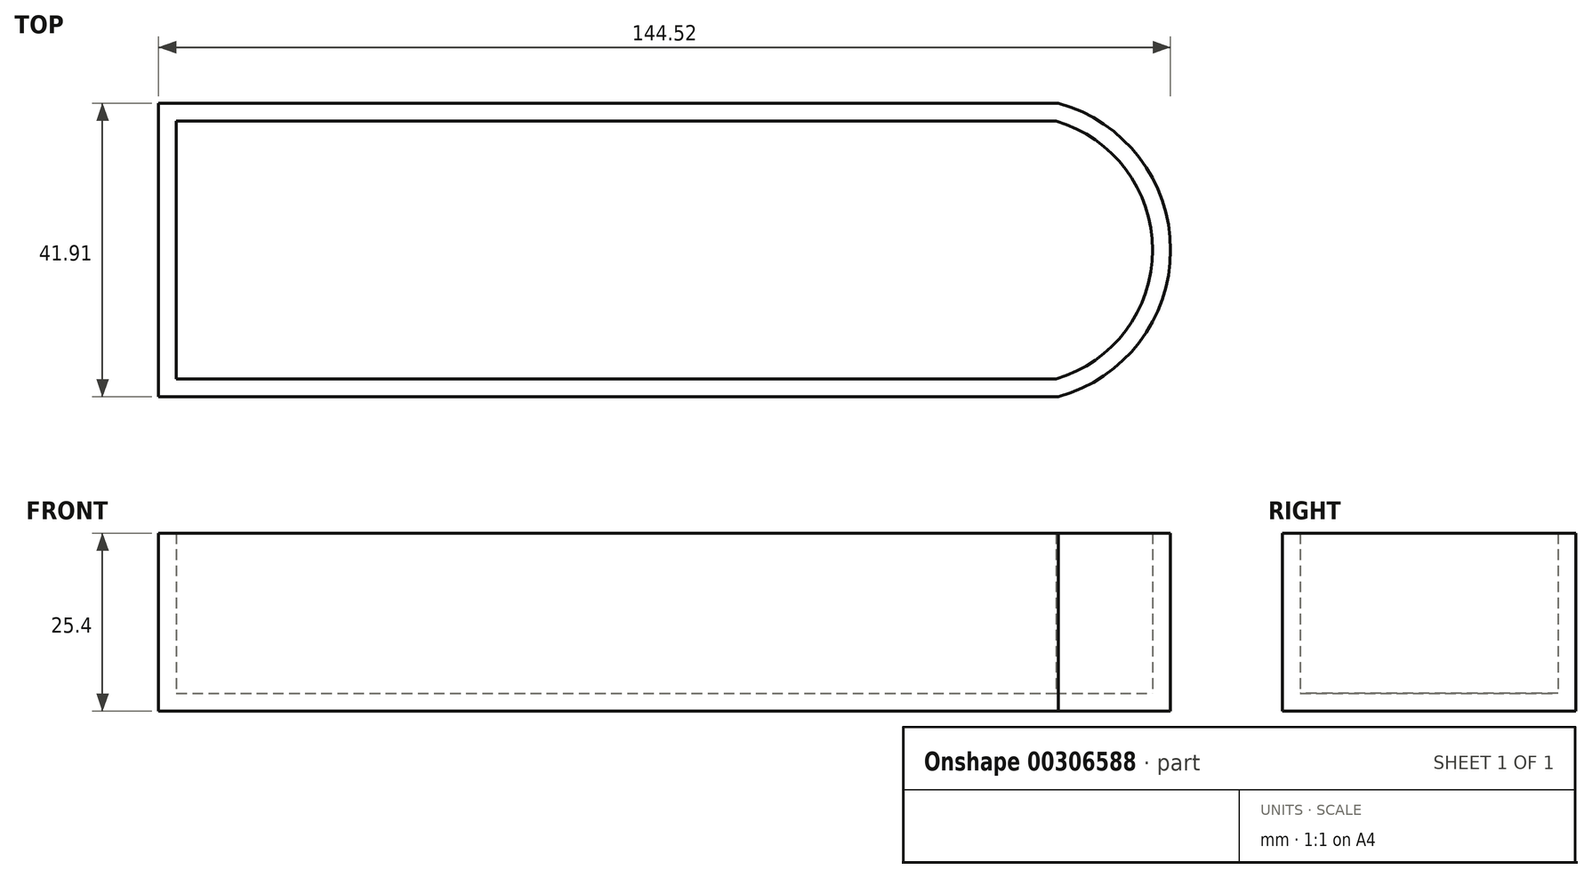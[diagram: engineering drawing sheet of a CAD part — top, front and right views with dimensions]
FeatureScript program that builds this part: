
annotation { "Feature Type Name" : "Feature", "Feature Type Description" : "" }
export const myFeature = defineFeature(function(context is Context, id is Id, definition is map)
    precondition{}
    {
        {
            var Q0;
            Q0=qCreatedBy(makeId("Top.planeOp"),FACE);
            var sketch = newSketch(context, id + "F0", { "sketchPlane" : qUnion([Q0])});
            skLineSegment(sketch, "E0.bottom", {"start": v(-62.74, 49.78) * mm, "end": v(65.79, 49.78) * mm});
            skLineSegment(sketch, "E0.top", {"start": v(-62.74, 7.87) * mm, "end": v(65.79, 7.87) * mm});
            skLineSegment(sketch, "E0.left", {"start": v(-62.74, 49.78) * mm, "end": v(-62.74, 7.87) * mm});
            skLineSegment(sketch, "E0.right", {"start": v(65.79, 49.78) * mm, "end": v(65.79, 7.87) * mm});
            skArc(sketch, "E1", {"start": v(65.79, 7.87) * mm, "mid": v(81.78, 28.83) * mm, "end": v(65.79, 49.78) * mm});
            skSolve(sketch);
        }
        {
            var Q0;
            Q0=makeQuery(id+"F0.imprint","IMPRINT",FACE,{"disambiguationData":[TD([[makeQuery(id+"F0.imprint","IMPRINT",EDGE,{"derivedFrom":sQuery(id+"F0.wireOp",EDGE,"E0.bottom")}),-1.0]])]});
            var Q1;
            Q1=makeQuery(id+"F0.imprint","IMPRINT",FACE,{"disambiguationData":[TD([[makeQuery(id+"F0.imprint","IMPRINT",EDGE,{"derivedFrom":sQuery(id+"F0.wireOp",EDGE,"E0.right")}),1.0]])]});
            extrude(context, id + "F1", {"entities" : qUnion([Q0, Q1]), "depth" : 25.4 * mm});
        }
        {
            var Q0;
            Q0=makeQuery(id+"F1.opExtrude","CAP_FACE",FACE,{"disambiguationData":[OSD([sQuery(id+"F0.wireOp",EDGE,"E0.bottom"),sQuery(id+"F0.wireOp",EDGE,"E0.top"),sQuery(id+"F0.wireOp",EDGE,"E0.left"),sQuery(id+"F0.wireOp",EDGE,"E1")])],"isStart":false});
            shell(context, id + "F2", {"entities" : qUnion([Q0]), "thickness" : 2.54 * mm});
        }
    });
